# Revit family: Gira_206705
name_source: partatom
category: Elektroinstallationen
revit_build: Autodesk Revit 2017 (Build: 20160225_1515(x64)
units: mm (PartAtom-declared; Revit-internal decimal feet)

## family parameters
Basisbauteil = Fläche
Beim Laden mit Abzugskörper schneiden = Nein
Bemaßung runder Anschluss = Durchmesser verwenden
Beschriftungsausrichtung beibehalten = Ja
Gemeinsam genutzt = Nein
Raumberechnungspunkt = Nein
Teiletyp = Normal

## types (1)
- Gira G1 230 V Gira G1 G Schwarz
    Andere Bussysteme = eNet
    Ausführung der Oberfläche = nicht zutreffend
    BIM = https://media.stage.bim.site
    BIMSITE_PRODUCT_ID = 1566026f7d7fcd12f15de7114faade05d222c1a9
    Beschreibung = Gira G1 230 V  Glas Schwarz Der Gira G1 ist ein multifunktionales Raumbediengerät zur Visualisierung und Bedienung vielfältiger Gebäudefunktionen. Zum Einsatz im KNX System und im Gira Türkommunikations-System oder als Client. Der jeweilige Funktionsumfang hängt von der verwendeten Firmware ab.  Den genauen Funktionsumfang entnehmen Sie bitte dem Gira Onlinekatalog sowie der technischen Gerätedokumentation.  Merkmale:  Die Bedienung erfolgt über ein gestenfähiges Multitouchdisplay.  Anbindung und Kommunikation ist variantenabhängig über LAN oder WLAN.  Integrierter Lautsprecher.  Integriertes Mikrofon mit Echokompensation.    Einsatzmöglichkeiten und Kombinationen:  Der Gira G1 als multifunktionales Raumbediengerät stellt folgende Funktionen bzw. Kombinationen von Funktionen zur Verfügung:  KNX Raumbediengerät  Wohnungsstation Video  Client für folgende Systeme   Server - HomeServer – eNet – X1- Sicherheitssystem Alarm Connect  Einbindung von Internetdiensten Eigenschaften als KNX Raumbediengerät:  Intuitiv bedienbare und durch den Endbenutzer anpassbare Benutzeroberfläche.  Schalten, Tasten, Dimmen (relativ u. absolut), Dimmen (inkl. Dimmen RGB, RGBW u. Tunable White) Jalousie- und Rollladensteuerung, Wertgeber, Szenennebenstelle.  Statusanzeige, Anzeige von Datum und Uhrzeit, Anzeige von Innen- und Außentemperatur.  Bis zu 150 Funktionen (sechs Funktionsordner bzw. Räume mit jeweils bis zu 25 Funktionen).  Bis zu 125 Wochen-Zeitschaltuhren mit jeweils 10 Schaltzeiten.  Raumtemperaturregler in Kombination mit dem optional erhältlicher Temperaturfühlermodul oder KNX Geräten zur Raumtemperaturmessung, z. B. Tastsensor 3 Komfort.  Betriebsmodi: Komfort, Stand-by, Nacht und Frost- bzw. Hitzeschutz mit jeweils eigenen Temperatursollwerten (für Heizen und bzw. oder Kühlen).  Betriebsmodi individuell anpassbar.  Eine Heizungsuhr als Wochen-Zeitschaltuhr mit 28 Schaltzeiten.  Raumtemperaturregler-Nebenstelle zur Ansteuerung von Klimaanlagen (Fancoil) in Verbindung mit einem KNX Gateway für Klimaanlagen. Eigenschaften als Wohnungsstation Video:  Kameraumschaltung: gezielte Anwahl der angeschlossenen Farbkameras.   Ansteuerung des Türöffners.  Rufton ein- und ausschalten.  Rufton wählbar aus 10 Melodien. Eigenschaften als Wohnungsstation mit SIP-Client:  Client Funktion für SIP Fremdsysteme von z. B. Comelit, TCS, SCHÜCO  SIP Direct calls oder über Registrar möglich  64 Internrufe möglich z. B. zum Concierge  Early Media Unterstützung für Videobild Einbindung von Internetdiensten:  Gira Wetterportal: Anzeige der Wetterprognose für bis zu fünf Orte (Internetverbindung erforderlich). Der Gira G1 kann auch als Client für folgende Systeme   Server eingesetzt werden::  HomeServer Client  eNet Client  X1 Client  Sicherheitssystem Alarm Connect  In der Funktion als Client stehen die Funktionen des KNX Raumbediengeräts nicht zur Verfügung. Den genauen Funktionsumfang entnehmen Sie bitte dem Gira Onlinekatalog sowie der technischen Gerätedokumentation.  Gira G1 mit Unterputz-Anschlussmodul 230 V WLAN.  Datenkommunikation über WLAN.  Hinweise :  Nur zur Verwendung im Innenbereich geeignet.  Empfohlene Montagehöhe: 150 cm ab Fußboden.  Die Montage erfolgt auf eine tiefe Gerätedose (Empfehlung Elektronikdose bei LAN-Anschluss).  Die Kommunikation zur KNX Installation erfolgt ausschließlich über den KNXnet IP Standard.  Zur Anbindung des Gira G1 PoE an die KNX Installation muss ein KNX IP-Router verwendet werden. Es können mehrere Gira G1 an einem KNX IP-Router betrieben werden.  Zur Anbindung des Gira G1 230 V oder G1 24 V an die KNX Installation ist ein Gira KNX IP-Router (ab Firmwareversion 3) erforderlich um eine zuverlässige Kommunikation im WLAN sicherzustellen. Hierzu ist der Gira KNX IP-Router (ab Firmwareversion 3) speziell mit der Zusatzfunktion Zuverlässige Datenkommunikation" ausgestattet. Es können mehrere Gira G1 an einem Gira KNX IP-Router (ab Firmwareversion 3) betrieben werden.  Hardware ab Indexstand I08 für KNX Secure vorbereitet (zusätzliches Firmeware-Update erforderlich).  Inbetriebnahme im KNX System ab ETS 5.5 oder höher.  Als Wohnungsstation nutzbar in Verbindung mit TKS-IP-Gateway.  Bitte beachten Sie bei der Planung der Anlage die technischen Informationen zur Netzwerkplanung in der Gerätedokumentation.  Für Firmware-Updates wird der Gira Projekt Assistent (GPA) benötigt. Der GPA ist kostenlos im Gira Downloadbereich verfügbar.  Zur Nutzung der Zeitschaltuhren ist entweder eine Internetverbindung zu einem NTP-Zeitserver oder ein entsprechender KNX Zeitgeber (z.B. Gira Wetterstation Plus 2074 00) erforderlich.  Für die Montage des Unterputz-Anschlussmoduls PoE wird die Verwendung einer Elektronikdose empfohlen.  Es wird ein handelsüblicher PoE-fähiger Switch bzw. Router oder ein PoE-Injector benötigt."
    Bussystem Funkbus = Nein
    Bussystem KNX = Ja
    Bussystem KNX-Funk = Nein
    Bussystem LON = Nein
    Bussystem Powernet = Nein
    DCF77 Empfänger integriert = Nein
    Datenblatt = https://media.stage.bim.site
    Datenblatt 1 = https://media.stage.bim.site
    Farbe = schwarz
    GTIN = 4010337014294
    HAN = 206705
    HeinzeBIM = https://www.heinze.de
    Hersteller = Gira
    IR-Sensor = Nein
    Kosten = 0 $
    Mit Busankopplung = Nein
    Mit Diebstahl-/Demontageschutz = Ja
    Mit Display = Ja
    Montageart = Unterputz
    Oberfläche Text = sonstige
    Produktseite = https://media.stage.bim.site
    Präsenztaster = Nein
    Schutzart (IP) = IP21
    Status-LED = Ja
    Temperaturregler = Ja
    Transparent = Nein
    Typname = Gira G1 230 V Gira G1 G Schwarz
    URL = https://www.gira.de
    Vorgabe-Ansicht = 1219 mm
    Werkstoff Text = sonstige
    Werkstoffgüte = sonstige
    Zentrale Funktionseinheit für Sender/Aktoren = Ja
    material_black = Black
    material_white = White

## geometry (parser evidence)
native form markers: Sweep x3
no freeform markers — native parametric forms only
